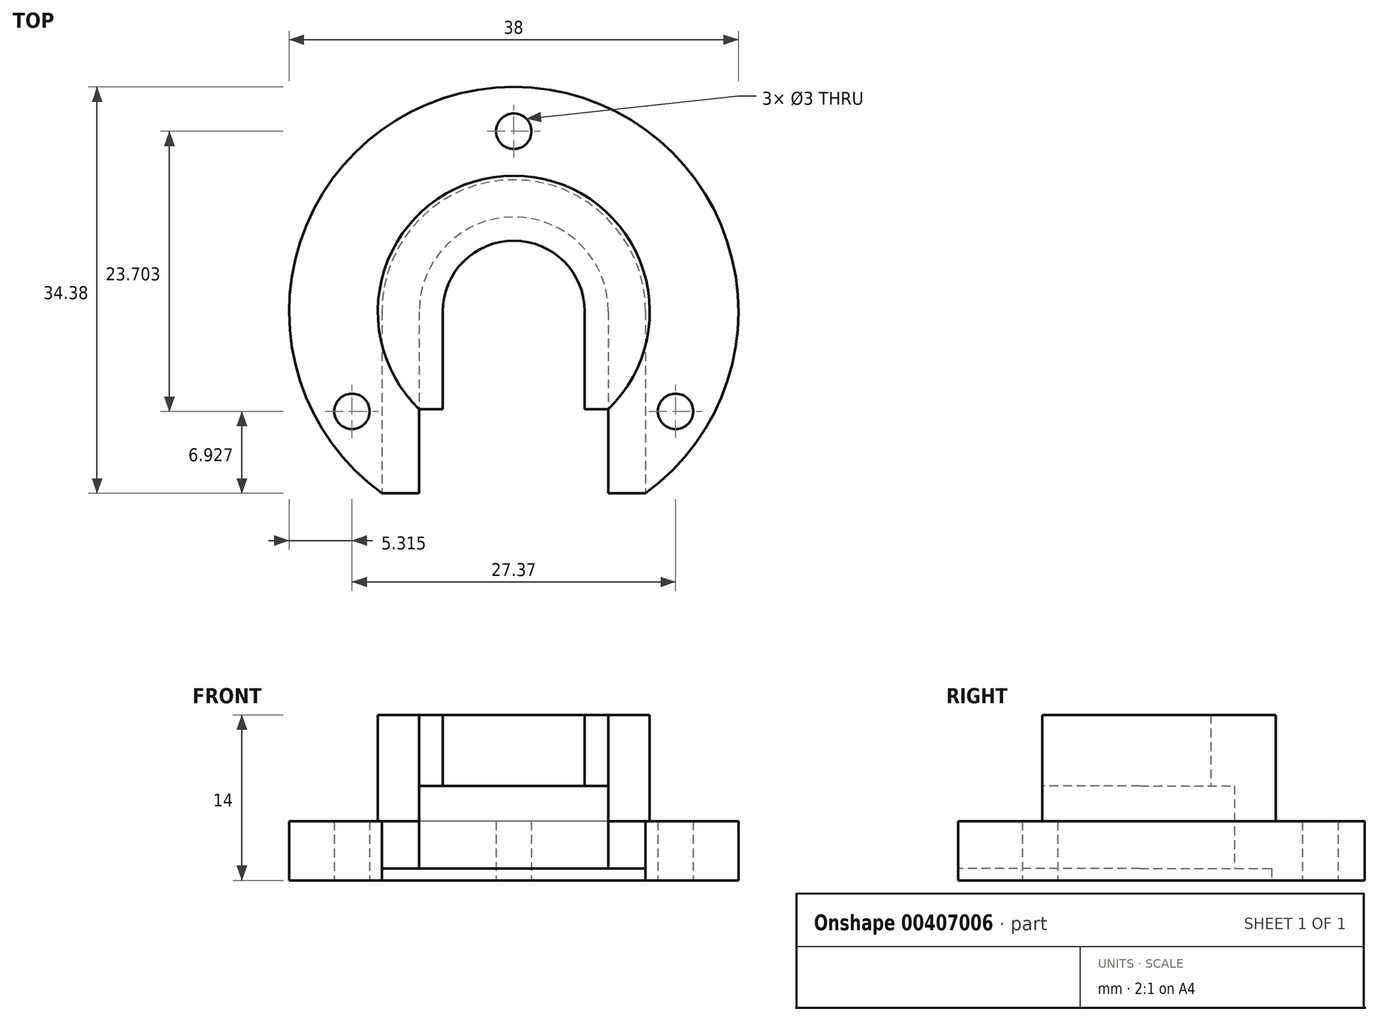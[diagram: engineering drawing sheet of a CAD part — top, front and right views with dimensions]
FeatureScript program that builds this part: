
annotation { "Feature Type Name" : "Feature", "Feature Type Description" : "" }
export const myFeature = defineFeature(function(context is Context, id is Id, definition is map)
    precondition{}
    {
        {
            var Q0;
            Q0=qCreatedBy(makeId("Top.planeOp"),FACE);
            var sketch = newSketch(context, id + "F0", { "sketchPlane" : qUnion([Q0])});
            skCircle(sketch, "E0", {"center": v(0, 0) * mm, "radius": 11.15 * mm});
            skCircle(sketch, "E1", {"center": v(0, 0) * mm, "radius": 8 * mm});
            skCircle(sketch, "E2", {"center": v(0, 0) * mm, "radius": 6 * mm});
            skCircle(sketch, "E3", {"center": v(0, 0) * mm, "radius": 11.5 * mm});
            skLineSegment(sketch, "E4.bottom", {"start": v(-6, 0) * mm, "end": v(6, 0) * mm});
            skLineSegment(sketch, "E4.top", {"start": v(-6, -28.3) * mm, "end": v(6, -28.3) * mm});
            skLineSegment(sketch, "E4.left", {"start": v(-6, 0) * mm, "end": v(-6, -28.3) * mm});
            skLineSegment(sketch, "E4.right", {"start": v(6, 0) * mm, "end": v(6, -28.3) * mm});
            skCircle(sketch, "E5", {"center": v(0, 0) * mm, "radius": 19 * mm});
            skLineSegment(sketch, "E6.bottom", {"start": v(-8, 0) * mm, "end": v(8, 0) * mm});
            skLineSegment(sketch, "E6.top", {"start": v(-8, -18.75) * mm, "end": v(8, -18.75) * mm});
            skLineSegment(sketch, "E6.left", {"start": v(-8, 0) * mm, "end": v(-8, -18.75) * mm});
            skLineSegment(sketch, "E6.right", {"start": v(8, 0) * mm, "end": v(8, -18.75) * mm});
            skLineSegment(sketch, "E7.bottom", {"start": v(-11.15, 0) * mm, "end": v(11.15, 0) * mm});
            skLineSegment(sketch, "E7.top", {"start": v(-11.15, -28.89) * mm, "end": v(11.15, -28.89) * mm});
            skLineSegment(sketch, "E7.left", {"start": v(-11.15, 0) * mm, "end": v(-11.15, -28.89) * mm});
            skLineSegment(sketch, "E7.right", {"start": v(11.15, 0) * mm, "end": v(11.15, -28.89) * mm});
            skCircle(sketch, "E8", {"center": v(0, 15.25) * mm, "radius": 1.5 * mm});
            skLineSegment(sketch, "E9", {"start": v(0, 11.5) * mm, "end": v(0, 19) * mm, "construction": true});
            skCircle(sketch, "E10.1.0", {"center": v(-13.68, -8.45) * mm, "radius": 1.5 * mm});
            skCircle(sketch, "E10.2.0", {"center": v(13.68, -8.45) * mm, "radius": 1.5 * mm});
            skPoint(sketch, "E10.center", {"position": v(0, -0.55) * mm});
            skLineSegment(sketch, "E11", {"start": v(-11.15, -15.38) * mm, "end": v(-8, -15.38) * mm});
            skLineSegment(sketch, "E12.MirrorCS", {"start": v(11.15, -15.38) * mm, "end": v(8, -15.38) * mm});
            skLineSegment(sketch, "E13", {"start": v(-8, -8.26) * mm, "end": v(-6, -8.26) * mm});
            skLineSegment(sketch, "E14", {"start": v(8, -8.26) * mm, "end": v(6, -8.26) * mm});
            skSolve(sketch);
        }
        {
            var Q0;
            {var subQ0=sQuery(id+"F0.wireOp",EDGE,"E7.left");var subQ1=sQuery(id+"F0.wireOp",EDGE,"E3");var subQ2=makeQuery(id+"F0.imprint","INTERSECT",VERTEX,{"derivedFrom":[subQ1,subQ0]});Q0=makeQuery(id+"F0.imprint","IMPRINT",FACE,{"disambiguationData":[TD([[makeQuery(id+"F0.imprint","IMPRINT",EDGE,{"disambiguationData":[TD([[subQ2,1.0]])],"derivedFrom":subQ1}),-1.0]])]});}
            var Q1;
            {var subQ0=sQuery(id+"F0.wireOp",EDGE,"E7.bottom");var subQ1=sQuery(id+"F0.wireOp",EDGE,"E0");var subQ2=makeQuery(id+"F0.imprint","INTERSECT",VERTEX,{"derivedFrom":[subQ1,subQ0,sQuery(id+"F0.wireOp",EDGE,"E7.left")]});Q1=makeQuery(id+"F0.imprint","IMPRINT",FACE,{"disambiguationData":[TD([[makeQuery(id+"F0.imprint","IMPRINT",EDGE,{"disambiguationData":[TD([[subQ2,1.0]])],"derivedFrom":subQ1}),1.0]])]});}
            var Q2;
            {var subQ0=sQuery(id+"F0.wireOp",EDGE,"E7.left");var subQ6=sQuery(id+"F0.wireOp",EDGE,"E3");var subQ7=makeQuery(id+"F0.imprint","INTERSECT",VERTEX,{"derivedFrom":[subQ6,subQ0]});Q2=makeQuery(id+"F0.imprint","IMPRINT",FACE,{"disambiguationData":[TD([[makeQuery(id+"F0.imprint","IMPRINT",EDGE,{"disambiguationData":[TD([[subQ7,1.0]])],"derivedFrom":subQ6}),1.0]])]});}
            var Q3;
            {var subQ0=sQuery(id+"F0.wireOp",EDGE,"E7.bottom");var subQ1=sQuery(id+"F0.wireOp",EDGE,"E1");var subQ2=makeQuery(id+"F0.imprint","INTERSECT",VERTEX,{"derivedFrom":[subQ1,sQuery(id+"F0.wireOp",EDGE,"E6.left"),subQ0]});Q3=makeQuery(id+"F0.imprint","IMPRINT",FACE,{"disambiguationData":[TD([[makeQuery(id+"F0.imprint","IMPRINT",EDGE,{"disambiguationData":[TD([[subQ2,1.0]])],"derivedFrom":subQ1}),1.0]])]});}
            var Q4;
            {var subQ1=sQuery(id+"F0.wireOp",EDGE,"E0");var subQ3=sQuery(id+"F0.wireOp",EDGE,"E6.left");var subQ4=makeQuery(id+"F0.imprint","INTERSECT",VERTEX,{"derivedFrom":[subQ1,subQ3]});Q4=makeQuery(id+"F0.imprint","IMPRINT",FACE,{"disambiguationData":[TD([[makeQuery(id+"F0.imprint","IMPRINT",EDGE,{"disambiguationData":[TD([[subQ4,1.0]])],"derivedFrom":subQ1}),1.0]])]});}
            var Q5;
            {var subQ0=sQuery(id+"F0.wireOp",EDGE,"E6.left");var subQ1=sQuery(id+"F0.wireOp",EDGE,"E3");var subQ2=makeQuery(id+"F0.imprint","INTERSECT",VERTEX,{"derivedFrom":[subQ1,subQ0]});Q5=makeQuery(id+"F0.imprint","IMPRINT",FACE,{"disambiguationData":[TD([[makeQuery(id+"F0.imprint","IMPRINT",EDGE,{"disambiguationData":[TD([[subQ2,1.0]])],"derivedFrom":subQ1}),-1.0]])]});}
            var Q6;
            {var subQ3=sQuery(id+"F0.wireOp",EDGE,"E6.left");var subQ5=sQuery(id+"F0.wireOp",EDGE,"E3");var subQ6=makeQuery(id+"F0.imprint","INTERSECT",VERTEX,{"derivedFrom":[subQ5,subQ3]});Q6=makeQuery(id+"F0.imprint","IMPRINT",FACE,{"disambiguationData":[TD([[makeQuery(id+"F0.imprint","IMPRINT",EDGE,{"disambiguationData":[TD([[subQ6,1.0]])],"derivedFrom":subQ5}),1.0]])]});}
            var Q7;
            {var subQ0=sQuery(id+"F0.wireOp",EDGE,"E6.left");var subQ1=sQuery(id+"F0.wireOp",EDGE,"E3");var subQ2=makeQuery(id+"F0.imprint","INTERSECT",VERTEX,{"derivedFrom":[subQ1,subQ0]});Q7=makeQuery(id+"F0.imprint","IMPRINT",FACE,{"disambiguationData":[TD([[makeQuery(id+"F0.imprint","IMPRINT",EDGE,{"disambiguationData":[TD([[subQ2,-1.0]])],"derivedFrom":subQ1}),-1.0]])]});}
            var Q8;
            {var subQ0=sQuery(id+"F0.wireOp",EDGE,"E6.left");var subQ1=sQuery(id+"F0.wireOp",EDGE,"E0");var subQ2=makeQuery(id+"F0.imprint","INTERSECT",VERTEX,{"derivedFrom":[subQ1,subQ0]});Q8=makeQuery(id+"F0.imprint","IMPRINT",FACE,{"disambiguationData":[TD([[makeQuery(id+"F0.imprint","IMPRINT",EDGE,{"disambiguationData":[TD([[subQ2,-1.0]])],"derivedFrom":subQ1}),-1.0]])]});}
            var Q9;
            {var subQ0=sQuery(id+"F0.wireOp",EDGE,"E6.left");var subQ1=sQuery(id+"F0.wireOp",EDGE,"E0");var subQ2=makeQuery(id+"F0.imprint","INTERSECT",VERTEX,{"derivedFrom":[subQ1,subQ0]});Q9=makeQuery(id+"F0.imprint","IMPRINT",FACE,{"disambiguationData":[TD([[makeQuery(id+"F0.imprint","IMPRINT",EDGE,{"disambiguationData":[TD([[subQ2,-1.0]])],"derivedFrom":subQ1}),1.0]])]});}
            var Q10;
            {var subQ1=sQuery(id+"F0.wireOp",EDGE,"E1");var subQ3=sQuery(id+"F0.wireOp",EDGE,"E4.left");var subQ4=makeQuery(id+"F0.imprint","INTERSECT",VERTEX,{"derivedFrom":[subQ1,subQ3]});Q10=makeQuery(id+"F0.imprint","IMPRINT",FACE,{"disambiguationData":[TD([[makeQuery(id+"F0.imprint","IMPRINT",EDGE,{"disambiguationData":[TD([[subQ4,1.0]])],"derivedFrom":subQ1}),1.0]])]});}
            var Q11;
            {var subQ1=sQuery(id+"F0.wireOp",EDGE,"E1");var subQ3=sQuery(id+"F0.wireOp",EDGE,"E4.right");var subQ4=makeQuery(id+"F0.imprint","INTERSECT",VERTEX,{"derivedFrom":[subQ1,subQ3]});Q11=makeQuery(id+"F0.imprint","IMPRINT",FACE,{"disambiguationData":[TD([[makeQuery(id+"F0.imprint","IMPRINT",EDGE,{"disambiguationData":[TD([[subQ4,-1.0]])],"derivedFrom":subQ1}),1.0]])]});}
            var Q12;
            {var subQ0=sQuery(id+"F0.wireOp",EDGE,"E4.right");var subQ1=sQuery(id+"F0.wireOp",EDGE,"E0");var subQ2=makeQuery(id+"F0.imprint","INTERSECT",VERTEX,{"derivedFrom":[subQ1,subQ0]});Q12=makeQuery(id+"F0.imprint","IMPRINT",FACE,{"disambiguationData":[TD([[makeQuery(id+"F0.imprint","IMPRINT",EDGE,{"disambiguationData":[TD([[subQ2,-1.0]])],"derivedFrom":subQ1}),1.0]])]});}
            var Q13;
            {var subQ1=sQuery(id+"F0.wireOp",EDGE,"E0");var subQ3=sQuery(id+"F0.wireOp",EDGE,"E6.right");var subQ4=makeQuery(id+"F0.imprint","INTERSECT",VERTEX,{"derivedFrom":[subQ1,subQ3]});Q13=makeQuery(id+"F0.imprint","IMPRINT",FACE,{"disambiguationData":[TD([[makeQuery(id+"F0.imprint","IMPRINT",EDGE,{"disambiguationData":[TD([[subQ4,-1.0]])],"derivedFrom":subQ1}),1.0]])]});}
            var Q14;
            {var subQ0=sQuery(id+"F0.wireOp",EDGE,"E6.right");var subQ1=sQuery(id+"F0.wireOp",EDGE,"E3");var subQ2=makeQuery(id+"F0.imprint","INTERSECT",VERTEX,{"derivedFrom":[subQ1,subQ0]});Q14=makeQuery(id+"F0.imprint","IMPRINT",FACE,{"disambiguationData":[TD([[makeQuery(id+"F0.imprint","IMPRINT",EDGE,{"disambiguationData":[TD([[subQ2,-1.0]])],"derivedFrom":subQ1}),-1.0]])]});}
            var Q15;
            {var subQ0=sQuery(id+"F0.wireOp",EDGE,"E4.right");var subQ1=sQuery(id+"F0.wireOp",EDGE,"E3");var subQ2=makeQuery(id+"F0.imprint","INTERSECT",VERTEX,{"derivedFrom":[subQ1,subQ0]});Q15=makeQuery(id+"F0.imprint","IMPRINT",FACE,{"disambiguationData":[TD([[makeQuery(id+"F0.imprint","IMPRINT",EDGE,{"disambiguationData":[TD([[subQ2,-1.0]])],"derivedFrom":subQ1}),-1.0]])]});}
            var Q16;
            {var subQ0=sQuery(id+"F0.wireOp",EDGE,"E4.right");var subQ1=sQuery(id+"F0.wireOp",EDGE,"E0");var subQ2=makeQuery(id+"F0.imprint","INTERSECT",VERTEX,{"derivedFrom":[subQ1,subQ0]});Q16=makeQuery(id+"F0.imprint","IMPRINT",FACE,{"disambiguationData":[TD([[makeQuery(id+"F0.imprint","IMPRINT",EDGE,{"disambiguationData":[TD([[subQ2,-1.0]])],"derivedFrom":subQ1}),-1.0]])]});}
            var Q17;
            {var subQ3=sQuery(id+"F0.wireOp",EDGE,"E6.right");var subQ5=sQuery(id+"F0.wireOp",EDGE,"E3");var subQ6=makeQuery(id+"F0.imprint","INTERSECT",VERTEX,{"derivedFrom":[subQ5,subQ3]});Q17=makeQuery(id+"F0.imprint","IMPRINT",FACE,{"disambiguationData":[TD([[makeQuery(id+"F0.imprint","IMPRINT",EDGE,{"disambiguationData":[TD([[subQ6,-1.0]])],"derivedFrom":subQ5}),1.0]])]});}
            var Q18;
            Q18=sQuery(id+"F0.wireOp",EDGE,"E5");
            extrude(context, id + "F1", {"entities" : qUnion([Q0, Q1, Q2, Q3, Q4, Q5, Q6, Q7, Q8, Q9, Q10, Q11, Q12, Q13, Q14, Q15, Q16, Q17]), "surfaceEntities" : qUnion([Q18]), "depth" : 5 * mm});
        }
        {
            var Q0;
            {var subQ0=sQuery(id+"F0.wireOp",EDGE,"E7.left");var subQ6=sQuery(id+"F0.wireOp",EDGE,"E3");var subQ7=makeQuery(id+"F0.imprint","INTERSECT",VERTEX,{"derivedFrom":[subQ6,subQ0]});Q0=makeQuery(id+"F0.imprint","IMPRINT",FACE,{"disambiguationData":[TD([[makeQuery(id+"F0.imprint","IMPRINT",EDGE,{"disambiguationData":[TD([[subQ7,1.0]])],"derivedFrom":subQ6}),1.0]])]});}
            var Q1;
            {var subQ0=sQuery(id+"F0.wireOp",EDGE,"E7.bottom");var subQ1=sQuery(id+"F0.wireOp",EDGE,"E0");var subQ2=makeQuery(id+"F0.imprint","INTERSECT",VERTEX,{"derivedFrom":[subQ1,subQ0,sQuery(id+"F0.wireOp",EDGE,"E7.left")]});Q1=makeQuery(id+"F0.imprint","IMPRINT",FACE,{"disambiguationData":[TD([[makeQuery(id+"F0.imprint","IMPRINT",EDGE,{"disambiguationData":[TD([[subQ2,1.0]])],"derivedFrom":subQ1}),1.0]])]});}
            var Q2;
            {var subQ1=sQuery(id+"F0.wireOp",EDGE,"E0");var subQ3=sQuery(id+"F0.wireOp",EDGE,"E6.right");var subQ4=makeQuery(id+"F0.imprint","INTERSECT",VERTEX,{"derivedFrom":[subQ1,subQ3]});Q2=makeQuery(id+"F0.imprint","IMPRINT",FACE,{"disambiguationData":[TD([[makeQuery(id+"F0.imprint","IMPRINT",EDGE,{"disambiguationData":[TD([[subQ4,-1.0]])],"derivedFrom":subQ1}),1.0]])]});}
            var Q3;
            {var subQ3=sQuery(id+"F0.wireOp",EDGE,"E6.right");var subQ5=sQuery(id+"F0.wireOp",EDGE,"E3");var subQ6=makeQuery(id+"F0.imprint","INTERSECT",VERTEX,{"derivedFrom":[subQ5,subQ3]});Q3=makeQuery(id+"F0.imprint","IMPRINT",FACE,{"disambiguationData":[TD([[makeQuery(id+"F0.imprint","IMPRINT",EDGE,{"disambiguationData":[TD([[subQ6,-1.0]])],"derivedFrom":subQ5}),1.0]])]});}
            var Q4;
            {var subQ1=sQuery(id+"F0.wireOp",EDGE,"E1");var subQ3=sQuery(id+"F0.wireOp",EDGE,"E4.right");var subQ4=makeQuery(id+"F0.imprint","INTERSECT",VERTEX,{"derivedFrom":[subQ1,subQ3]});Q4=makeQuery(id+"F0.imprint","IMPRINT",FACE,{"disambiguationData":[TD([[makeQuery(id+"F0.imprint","IMPRINT",EDGE,{"disambiguationData":[TD([[subQ4,-1.0]])],"derivedFrom":subQ1}),1.0]])]});}
            var Q5;
            {var subQ0=sQuery(id+"F0.wireOp",EDGE,"E7.bottom");var subQ1=sQuery(id+"F0.wireOp",EDGE,"E1");var subQ2=makeQuery(id+"F0.imprint","INTERSECT",VERTEX,{"derivedFrom":[subQ1,sQuery(id+"F0.wireOp",EDGE,"E6.left"),subQ0]});Q5=makeQuery(id+"F0.imprint","IMPRINT",FACE,{"disambiguationData":[TD([[makeQuery(id+"F0.imprint","IMPRINT",EDGE,{"disambiguationData":[TD([[subQ2,1.0]])],"derivedFrom":subQ1}),1.0]])]});}
            var Q6;
            {var subQ1=sQuery(id+"F0.wireOp",EDGE,"E1");var subQ3=sQuery(id+"F0.wireOp",EDGE,"E4.left");var subQ4=makeQuery(id+"F0.imprint","INTERSECT",VERTEX,{"derivedFrom":[subQ1,subQ3]});Q6=makeQuery(id+"F0.imprint","IMPRINT",FACE,{"disambiguationData":[TD([[makeQuery(id+"F0.imprint","IMPRINT",EDGE,{"disambiguationData":[TD([[subQ4,1.0]])],"derivedFrom":subQ1}),1.0]])]});}
            var Q7;
            {var subQ0=sQuery(id+"F0.wireOp",EDGE,"E6.left");var subQ1=sQuery(id+"F0.wireOp",EDGE,"E0");var subQ2=makeQuery(id+"F0.imprint","INTERSECT",VERTEX,{"derivedFrom":[subQ1,subQ0]});Q7=makeQuery(id+"F0.imprint","IMPRINT",FACE,{"disambiguationData":[TD([[makeQuery(id+"F0.imprint","IMPRINT",EDGE,{"disambiguationData":[TD([[subQ2,-1.0]])],"derivedFrom":subQ1}),1.0]])]});}
            var Q8;
            {var subQ1=sQuery(id+"F0.wireOp",EDGE,"E0");var subQ3=sQuery(id+"F0.wireOp",EDGE,"E6.left");var subQ4=makeQuery(id+"F0.imprint","INTERSECT",VERTEX,{"derivedFrom":[subQ1,subQ3]});Q8=makeQuery(id+"F0.imprint","IMPRINT",FACE,{"disambiguationData":[TD([[makeQuery(id+"F0.imprint","IMPRINT",EDGE,{"disambiguationData":[TD([[subQ4,1.0]])],"derivedFrom":subQ1}),1.0]])]});}
            var Q9;
            {var subQ3=sQuery(id+"F0.wireOp",EDGE,"E6.left");var subQ5=sQuery(id+"F0.wireOp",EDGE,"E3");var subQ6=makeQuery(id+"F0.imprint","INTERSECT",VERTEX,{"derivedFrom":[subQ5,subQ3]});Q9=makeQuery(id+"F0.imprint","IMPRINT",FACE,{"disambiguationData":[TD([[makeQuery(id+"F0.imprint","IMPRINT",EDGE,{"disambiguationData":[TD([[subQ6,1.0]])],"derivedFrom":subQ5}),1.0]])]});}
            var Q10;
            {var subQ0=sQuery(id+"F0.wireOp",EDGE,"E6.left");var subQ1=sQuery(id+"F0.wireOp",EDGE,"E0");var subQ2=makeQuery(id+"F0.imprint","INTERSECT",VERTEX,{"derivedFrom":[subQ1,subQ0]});Q10=makeQuery(id+"F0.imprint","IMPRINT",FACE,{"disambiguationData":[TD([[makeQuery(id+"F0.imprint","IMPRINT",EDGE,{"disambiguationData":[TD([[subQ2,-1.0]])],"derivedFrom":subQ1}),-1.0]])]});}
            var Q11;
            {var subQ0=sQuery(id+"F0.wireOp",EDGE,"E14");var subQ1=sQuery(id+"F0.wireOp",EDGE,"E0");var subQ2=makeQuery(id+"F0.imprint","INTERSECT",VERTEX,{"derivedFrom":[subQ1,subQ0]});Q11=makeQuery(id+"F0.imprint","IMPRINT",FACE,{"disambiguationData":[TD([[makeQuery(id+"F0.imprint","IMPRINT",EDGE,{"disambiguationData":[TD([[subQ2,-1.0]])],"derivedFrom":subQ1}),-1.0]])]});}
            var Q12;
            {var subQ3=sQuery(id+"F0.wireOp",EDGE,"E0");var subQ5=sQuery(id+"F0.wireOp",EDGE,"E14");var subQ9=makeQuery(id+"F0.imprint","INTERSECT",VERTEX,{"derivedFrom":[subQ3,subQ5]});Q12=makeQuery(id+"F0.imprint","IMPRINT",FACE,{"disambiguationData":[TD([[makeQuery(id+"F0.imprint","IMPRINT",EDGE,{"disambiguationData":[TD([[subQ9,-1.0]])],"derivedFrom":subQ3}),1.0]])]});}
            extrude(context, id + "F2", {"entities" : qUnion([Q0, Q1, Q2, Q3, Q4, Q5, Q6, Q7, Q8, Q9, Q10, Q11, Q12]), "operationType" : NewBodyOperationType.ADD, "depth" : 14 * mm});
        }
        {
            var Q0;
            {var subQ1=sQuery(id+"F0.wireOp",EDGE,"E1");var subQ3=sQuery(id+"F0.wireOp",EDGE,"E4.right");var subQ4=makeQuery(id+"F0.imprint","INTERSECT",VERTEX,{"derivedFrom":[subQ1,subQ3]});Q0=makeQuery(id+"F0.imprint","IMPRINT",FACE,{"disambiguationData":[TD([[makeQuery(id+"F0.imprint","IMPRINT",EDGE,{"disambiguationData":[TD([[subQ4,-1.0]])],"derivedFrom":subQ1}),1.0]])]});}
            var Q1;
            {var subQ0=sQuery(id+"F0.wireOp",EDGE,"E4.right");var subQ1=sQuery(id+"F0.wireOp",EDGE,"E0");var subQ2=makeQuery(id+"F0.imprint","INTERSECT",VERTEX,{"derivedFrom":[subQ1,subQ0]});Q1=makeQuery(id+"F0.imprint","IMPRINT",FACE,{"disambiguationData":[TD([[makeQuery(id+"F0.imprint","IMPRINT",EDGE,{"disambiguationData":[TD([[subQ2,-1.0]])],"derivedFrom":subQ1}),1.0]])]});}
            var Q2;
            {var subQ0=sQuery(id+"F0.wireOp",EDGE,"E4.right");var subQ1=sQuery(id+"F0.wireOp",EDGE,"E3");var subQ2=makeQuery(id+"F0.imprint","INTERSECT",VERTEX,{"derivedFrom":[subQ1,subQ0]});Q2=makeQuery(id+"F0.imprint","IMPRINT",FACE,{"disambiguationData":[TD([[makeQuery(id+"F0.imprint","IMPRINT",EDGE,{"disambiguationData":[TD([[subQ2,-1.0]])],"derivedFrom":subQ1}),-1.0]])]});}
            var Q3;
            {var subQ0=sQuery(id+"F0.wireOp",EDGE,"E5");var subQ1=sQuery(id+"F0.wireOp",EDGE,"E4.right");var subQ2=makeQuery(id+"F0.imprint","INTERSECT",VERTEX,{"derivedFrom":[subQ1,subQ0]});Q3=makeQuery(id+"F0.imprint","IMPRINT",FACE,{"disambiguationData":[TD([[makeQuery(id+"F0.imprint","IMPRINT",EDGE,{"disambiguationData":[TD([[subQ2,-1.0]])],"derivedFrom":subQ1}),1.0]])]});}
            var Q4;
            {var subQ0=sQuery(id+"F0.wireOp",EDGE,"E4.right");var subQ1=sQuery(id+"F0.wireOp",EDGE,"E0");var subQ2=makeQuery(id+"F0.imprint","INTERSECT",VERTEX,{"derivedFrom":[subQ1,subQ0]});Q4=makeQuery(id+"F0.imprint","IMPRINT",FACE,{"disambiguationData":[TD([[makeQuery(id+"F0.imprint","IMPRINT",EDGE,{"disambiguationData":[TD([[subQ2,-1.0]])],"derivedFrom":subQ1}),-1.0]])]});}
            var Q5;
            {var subQ0=sQuery(id+"F0.wireOp",EDGE,"E5");var subQ1=sQuery(id+"F0.wireOp",EDGE,"E4.left");var subQ2=makeQuery(id+"F0.imprint","INTERSECT",VERTEX,{"derivedFrom":[subQ1,subQ0]});Q5=makeQuery(id+"F0.imprint","IMPRINT",FACE,{"disambiguationData":[TD([[makeQuery(id+"F0.imprint","IMPRINT",EDGE,{"disambiguationData":[TD([[subQ2,-1.0]])],"derivedFrom":subQ1}),-1.0]])]});}
            var Q6;
            {var subQ0=sQuery(id+"F0.wireOp",EDGE,"E6.left");var subQ1=sQuery(id+"F0.wireOp",EDGE,"E3");var subQ2=makeQuery(id+"F0.imprint","INTERSECT",VERTEX,{"derivedFrom":[subQ1,subQ0]});Q6=makeQuery(id+"F0.imprint","IMPRINT",FACE,{"disambiguationData":[TD([[makeQuery(id+"F0.imprint","IMPRINT",EDGE,{"disambiguationData":[TD([[subQ2,-1.0]])],"derivedFrom":subQ1}),-1.0]])]});}
            var Q7;
            {var subQ0=sQuery(id+"F0.wireOp",EDGE,"E6.left");var subQ1=sQuery(id+"F0.wireOp",EDGE,"E0");var subQ2=makeQuery(id+"F0.imprint","INTERSECT",VERTEX,{"derivedFrom":[subQ1,subQ0]});Q7=makeQuery(id+"F0.imprint","IMPRINT",FACE,{"disambiguationData":[TD([[makeQuery(id+"F0.imprint","IMPRINT",EDGE,{"disambiguationData":[TD([[subQ2,-1.0]])],"derivedFrom":subQ1}),1.0]])]});}
            var Q8;
            {var subQ1=sQuery(id+"F0.wireOp",EDGE,"E1");var subQ3=sQuery(id+"F0.wireOp",EDGE,"E4.left");var subQ4=makeQuery(id+"F0.imprint","INTERSECT",VERTEX,{"derivedFrom":[subQ1,subQ3]});Q8=makeQuery(id+"F0.imprint","IMPRINT",FACE,{"disambiguationData":[TD([[makeQuery(id+"F0.imprint","IMPRINT",EDGE,{"disambiguationData":[TD([[subQ4,1.0]])],"derivedFrom":subQ1}),1.0]])]});}
            var Q9;
            {var subQ0=sQuery(id+"F0.wireOp",EDGE,"E6.left");var subQ1=sQuery(id+"F0.wireOp",EDGE,"E0");var subQ2=makeQuery(id+"F0.imprint","INTERSECT",VERTEX,{"derivedFrom":[subQ1,subQ0]});Q9=makeQuery(id+"F0.imprint","IMPRINT",FACE,{"disambiguationData":[TD([[makeQuery(id+"F0.imprint","IMPRINT",EDGE,{"disambiguationData":[TD([[subQ2,-1.0]])],"derivedFrom":subQ1}),-1.0]])]});}
            var Q10;
            {var subQ0=sQuery(id+"F0.wireOp",EDGE,"E7.bottom");var subQ1=sQuery(id+"F0.wireOp",EDGE,"E1");var subQ2=makeQuery(id+"F0.imprint","INTERSECT",VERTEX,{"derivedFrom":[subQ1,sQuery(id+"F0.wireOp",EDGE,"E6.left"),subQ0]});Q10=makeQuery(id+"F0.imprint","IMPRINT",FACE,{"disambiguationData":[TD([[makeQuery(id+"F0.imprint","IMPRINT",EDGE,{"disambiguationData":[TD([[subQ2,1.0]])],"derivedFrom":subQ1}),1.0]])]});}
            var Q11;
            {var subQ3=sQuery(id+"F0.wireOp",EDGE,"E0");var subQ5=sQuery(id+"F0.wireOp",EDGE,"E14");var subQ9=makeQuery(id+"F0.imprint","INTERSECT",VERTEX,{"derivedFrom":[subQ3,subQ5]});Q11=makeQuery(id+"F0.imprint","IMPRINT",FACE,{"disambiguationData":[TD([[makeQuery(id+"F0.imprint","IMPRINT",EDGE,{"disambiguationData":[TD([[subQ9,-1.0]])],"derivedFrom":subQ3}),1.0]])]});}
            var Q12;
            {var subQ0=sQuery(id+"F0.wireOp",EDGE,"E14");var subQ1=sQuery(id+"F0.wireOp",EDGE,"E0");var subQ2=makeQuery(id+"F0.imprint","INTERSECT",VERTEX,{"derivedFrom":[subQ1,subQ0]});Q12=makeQuery(id+"F0.imprint","IMPRINT",FACE,{"disambiguationData":[TD([[makeQuery(id+"F0.imprint","IMPRINT",EDGE,{"disambiguationData":[TD([[subQ2,-1.0]])],"derivedFrom":subQ1}),-1.0]])]});}
            extrude(context, id + "F3", {"entities" : qUnion([Q0, Q1, Q2, Q3, Q4, Q5, Q6, Q7, Q8, Q9, Q10, Q11, Q12]), "operationType" : NewBodyOperationType.REMOVE, "depth" : 8 * mm});
        }
        {
            var Q0;
            {var subQ1=sQuery(id+"F0.wireOp",EDGE,"E0");var subQ3=sQuery(id+"F0.wireOp",EDGE,"E6.right");var subQ4=makeQuery(id+"F0.imprint","INTERSECT",VERTEX,{"derivedFrom":[subQ1,subQ3]});Q0=makeQuery(id+"F0.imprint","IMPRINT",FACE,{"disambiguationData":[TD([[makeQuery(id+"F0.imprint","IMPRINT",EDGE,{"disambiguationData":[TD([[subQ4,-1.0]])],"derivedFrom":subQ1}),1.0]])]});}
            var Q1;
            {var subQ0=sQuery(id+"F0.wireOp",EDGE,"E6.right");var subQ1=sQuery(id+"F0.wireOp",EDGE,"E3");var subQ2=makeQuery(id+"F0.imprint","INTERSECT",VERTEX,{"derivedFrom":[subQ1,subQ0]});Q1=makeQuery(id+"F0.imprint","IMPRINT",FACE,{"disambiguationData":[TD([[makeQuery(id+"F0.imprint","IMPRINT",EDGE,{"disambiguationData":[TD([[subQ2,-1.0]])],"derivedFrom":subQ1}),-1.0]])]});}
            var Q2;
            {var subQ3=sQuery(id+"F0.wireOp",EDGE,"E6.right");var subQ5=sQuery(id+"F0.wireOp",EDGE,"E3");var subQ6=makeQuery(id+"F0.imprint","INTERSECT",VERTEX,{"derivedFrom":[subQ5,subQ3]});Q2=makeQuery(id+"F0.imprint","IMPRINT",FACE,{"disambiguationData":[TD([[makeQuery(id+"F0.imprint","IMPRINT",EDGE,{"disambiguationData":[TD([[subQ6,-1.0]])],"derivedFrom":subQ5}),1.0]])]});}
            var Q3;
            {var subQ0=sQuery(id+"F0.wireOp",EDGE,"E7.bottom");var subQ1=sQuery(id+"F0.wireOp",EDGE,"E0");var subQ2=makeQuery(id+"F0.imprint","INTERSECT",VERTEX,{"derivedFrom":[subQ1,subQ0,sQuery(id+"F0.wireOp",EDGE,"E7.left")]});Q3=makeQuery(id+"F0.imprint","IMPRINT",FACE,{"disambiguationData":[TD([[makeQuery(id+"F0.imprint","IMPRINT",EDGE,{"disambiguationData":[TD([[subQ2,1.0]])],"derivedFrom":subQ1}),1.0]])]});}
            var Q4;
            {var subQ1=sQuery(id+"F0.wireOp",EDGE,"E0");var subQ3=sQuery(id+"F0.wireOp",EDGE,"E6.left");var subQ4=makeQuery(id+"F0.imprint","INTERSECT",VERTEX,{"derivedFrom":[subQ1,subQ3]});Q4=makeQuery(id+"F0.imprint","IMPRINT",FACE,{"disambiguationData":[TD([[makeQuery(id+"F0.imprint","IMPRINT",EDGE,{"disambiguationData":[TD([[subQ4,1.0]])],"derivedFrom":subQ1}),1.0]])]});}
            var Q5;
            {var subQ3=sQuery(id+"F0.wireOp",EDGE,"E6.left");var subQ5=sQuery(id+"F0.wireOp",EDGE,"E3");var subQ6=makeQuery(id+"F0.imprint","INTERSECT",VERTEX,{"derivedFrom":[subQ5,subQ3]});Q5=makeQuery(id+"F0.imprint","IMPRINT",FACE,{"disambiguationData":[TD([[makeQuery(id+"F0.imprint","IMPRINT",EDGE,{"disambiguationData":[TD([[subQ6,1.0]])],"derivedFrom":subQ5}),1.0]])]});}
            var Q6;
            {var subQ0=sQuery(id+"F0.wireOp",EDGE,"E6.left");var subQ1=sQuery(id+"F0.wireOp",EDGE,"E3");var subQ2=makeQuery(id+"F0.imprint","INTERSECT",VERTEX,{"derivedFrom":[subQ1,subQ0]});Q6=makeQuery(id+"F0.imprint","IMPRINT",FACE,{"disambiguationData":[TD([[makeQuery(id+"F0.imprint","IMPRINT",EDGE,{"disambiguationData":[TD([[subQ2,1.0]])],"derivedFrom":subQ1}),-1.0]])]});}
            extrude(context, id + "F4", {"entities" : qUnion([Q0, Q1, Q2, Q3, Q4, Q5, Q6]), "operationType" : NewBodyOperationType.REMOVE, "depth" : 1 * mm});
        }
    });
